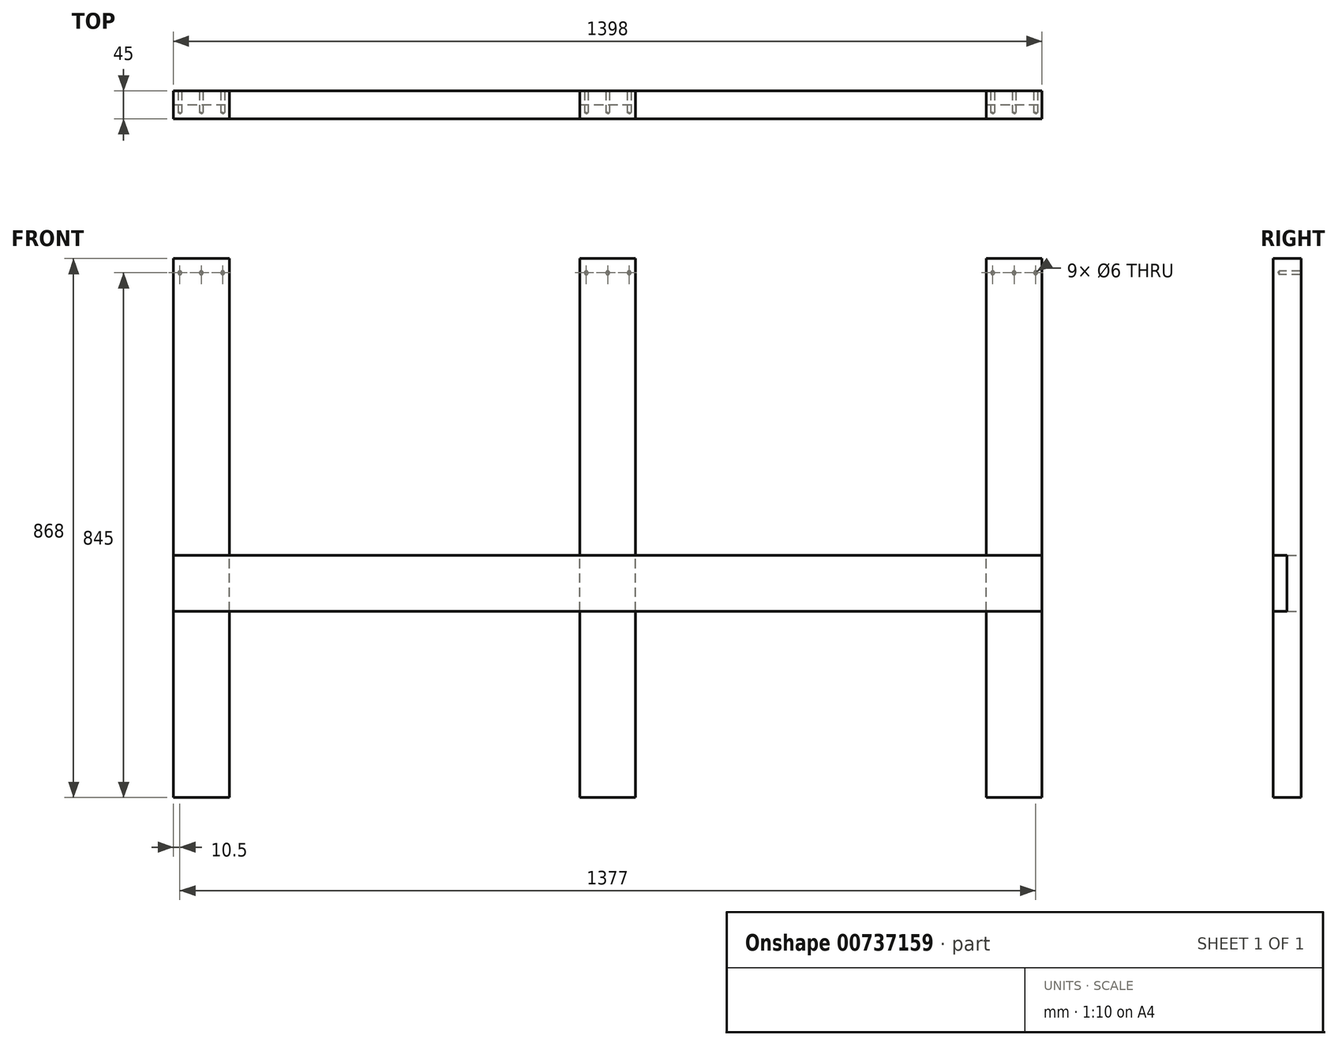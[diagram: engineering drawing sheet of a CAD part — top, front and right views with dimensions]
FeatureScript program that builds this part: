
annotation { "Feature Type Name" : "Feature", "Feature Type Description" : "" }
export const myFeature = defineFeature(function(context is Context, id is Id, definition is map)
    precondition{}
    {
        {
            var Q0;
            Q0=qCreatedBy(makeId("Front.planeOp"),FACE);
            var sketch = newSketch(context, id + "F0", { "sketchPlane" : qUnion([Q0])});
            skLineSegment(sketch, "E0.bottom", {"start": v(-609, 0) * mm, "end": v(-699, 0) * mm});
            skLineSegment(sketch, "E0.top", {"start": v(-609, 868) * mm, "end": v(-699, 868) * mm});
            skLineSegment(sketch, "E0.left", {"start": v(-609, 0) * mm, "end": v(-609, 868) * mm});
            skLineSegment(sketch, "E0.right", {"start": v(-699, 0) * mm, "end": v(-699, 868) * mm});
            skLineSegment(sketch, "E1.bottom", {"start": v(-45, 0) * mm, "end": v(45, 0) * mm});
            skLineSegment(sketch, "E1.top", {"start": v(-45, 868) * mm, "end": v(45, 868) * mm});
            skLineSegment(sketch, "E1.left", {"start": v(-45, 0) * mm, "end": v(-45, 868) * mm});
            skLineSegment(sketch, "E1.right", {"start": v(45, 0) * mm, "end": v(45, 868) * mm});
            skLineSegment(sketch, "E2.bottom", {"start": v(609, 0) * mm, "end": v(699, 0) * mm});
            skLineSegment(sketch, "E2.top", {"start": v(609, 868) * mm, "end": v(699, 868) * mm});
            skLineSegment(sketch, "E2.left", {"start": v(609, 0) * mm, "end": v(609, 868) * mm});
            skLineSegment(sketch, "E2.right", {"start": v(699, 0) * mm, "end": v(699, 868) * mm});
            skLineSegment(sketch, "E3", {"start": v(-609, 434) * mm, "end": v(-45, 434) * mm, "construction": true});
            skLineSegment(sketch, "E4", {"start": v(45, 434) * mm, "end": v(609, 434) * mm, "construction": true});
            skSolve(sketch);
        }
        {
            var Q0;
            Q0 = qSketchRegion(id + "F0", true);
            extrude(context, id + "F1", {"entities" : qUnion([Q0]), "depth" : 45 * mm, "offsetDistance" : 25 * mm});
        }
        {
            var Q0;
            Q0=makeQuery(id+"F1.opExtrude","CAP_FACE",FACE,{"disambiguationData":[OSD([sQuery(id+"F0.wireOp",EDGE,"E0.bottom"),sQuery(id+"F0.wireOp",EDGE,"E0.top"),sQuery(id+"F0.wireOp",EDGE,"E0.left"),sQuery(id+"F0.wireOp",EDGE,"E0.right")])],"isStart":false});
            var sketch = newSketch(context, id + "F2", { "sketchPlane" : qUnion([Q0])});
            skLineSegment(sketch, "E5.bottom", {"start": v(-699, 390) * mm, "end": v(699, 390) * mm});
            skLineSegment(sketch, "E5.top", {"start": v(-699, 300) * mm, "end": v(699, 300) * mm});
            skLineSegment(sketch, "E5.left", {"start": v(-699, 390) * mm, "end": v(-699, 300) * mm});
            skLineSegment(sketch, "E5.right", {"start": v(699, 390) * mm, "end": v(699, 300) * mm});
            skSolve(sketch);
        }
        {
            var Q0;
            Q0 = qSketchRegion(id + "F2", true);
            extrude(context, id + "F3", {"entities" : qUnion([Q0]), "operationType" : NewBodyOperationType.REMOVE, "oppositeDirection" : true, "depth" : (45 / 2) * mm, "offsetDistance" : 25 * mm});
        }
        {
            var Q0;
            {var subQ0=sQuery(id+"F0.wireOp",EDGE,"E0.bottom");var subQ1=sQuery(id+"F0.wireOp",EDGE,"E0.right");var subQ2=sQuery(id+"F0.wireOp",EDGE,"E0.left");Q0=makeQuery(id+"F3.boolean.opBoolean","SPLIT",FACE,{"disambiguationData":[TD([makeQuery(id+"F1.opExtrude","SWEPT_FACE",FACE,{"disambiguationData":[OSD([subQ0])]})])],"derivedFrom":makeQuery(id+"F1.opExtrude","CAP_FACE",FACE,{"disambiguationData":[OSD([subQ0,sQuery(id+"F0.wireOp",EDGE,"E0.top"),subQ2,subQ1])],"isStart":false})});}
            var sketch = newSketch(context, id + "F4", { "sketchPlane" : qUnion([Q0])});
            skLineSegment(sketch, "E6.0", {"start": v(-699, 390) * mm, "end": v(699, 390) * mm});
            skLineSegment(sketch, "E6.1", {"start": v(-699, 390) * mm, "end": v(-699, 300) * mm});
            skLineSegment(sketch, "E6.2", {"start": v(-699, 300) * mm, "end": v(699, 300) * mm});
            skLineSegment(sketch, "E6.3", {"start": v(699, 390) * mm, "end": v(699, 300) * mm});
            skSolve(sketch);
        }
        {
            var Q0;
            Q0 = qSketchRegion(id + "F4", true);
            extrude(context, id + "F5", {"entities" : qUnion([Q0]), "oppositeDirection" : true, "depth" : 45 * mm, "offsetDistance" : 25 * mm});
        }
        {
            var Q0;
            Q0=makeQuery(id+"F1.opExtrude","SWEPT_BODY",BODY,{"disambiguationData":[OSD([sQuery(id+"F0.wireOp",EDGE,"E0.bottom"),sQuery(id+"F0.wireOp",EDGE,"E0.top"),sQuery(id+"F0.wireOp",EDGE,"E0.left"),sQuery(id+"F0.wireOp",EDGE,"E0.right")])]});
            var Q1;
            Q1=makeQuery(id+"F1.opExtrude","SWEPT_BODY",BODY,{"disambiguationData":[OSD([sQuery(id+"F0.wireOp",EDGE,"E1.bottom"),sQuery(id+"F0.wireOp",EDGE,"E1.top"),sQuery(id+"F0.wireOp",EDGE,"E1.left"),sQuery(id+"F0.wireOp",EDGE,"E1.right")])]});
            var Q2;
            Q2=makeQuery(id+"F1.opExtrude","SWEPT_BODY",BODY,{"disambiguationData":[OSD([sQuery(id+"F0.wireOp",EDGE,"E2.bottom"),sQuery(id+"F0.wireOp",EDGE,"E2.top"),sQuery(id+"F0.wireOp",EDGE,"E2.left"),sQuery(id+"F0.wireOp",EDGE,"E2.right")])]});
            var Q3;
            Q3=makeQuery(id+"F5.opExtrude","SWEPT_BODY",BODY,{"disambiguationData":[OSD([sQuery(id+"F4.wireOp",EDGE,"E6.0"),sQuery(id+"F4.wireOp",EDGE,"E6.1"),sQuery(id+"F4.wireOp",EDGE,"E6.2"),sQuery(id+"F4.wireOp",EDGE,"E6.3")])]});
            booleanBodies(context, id + "F6", {"operationType" : BooleanOperationType.SUBTRACTION, "tools" : qUnion([Q0, Q1, Q2]), "targets" : qUnion([Q3]), "keepTools" : true});
        }
        {
            var Q0;
            Q0=makeQuery(id+"F1.opExtrude","CAP_FACE",FACE,{"disambiguationData":[OSD([sQuery(id+"F0.wireOp",EDGE,"E2.bottom"),sQuery(id+"F0.wireOp",EDGE,"E2.top"),sQuery(id+"F0.wireOp",EDGE,"E2.left"),sQuery(id+"F0.wireOp",EDGE,"E2.right")])],"isStart":true});
            var sketch = newSketch(context, id + "F7", { "sketchPlane" : qUnion([Q0])});
            skPoint(sketch, "E7", {"position": v(-688.5, 845) * mm});
            skPoint(sketch, "E8", {"position": v(-654, 845) * mm});
            skPoint(sketch, "E9", {"position": v(-619.5, 845) * mm});
            skPoint(sketch, "E10", {"position": v(-34.5, 845) * mm});
            skPoint(sketch, "E11", {"position": v(0, 845) * mm});
            skPoint(sketch, "E12", {"position": v(34.5, 845) * mm});
            skPoint(sketch, "E13", {"position": v(619.5, 845) * mm});
            skPoint(sketch, "E14", {"position": v(654, 845) * mm});
            skPoint(sketch, "E15", {"position": v(688.5, 845) * mm});
            skLineSegment(sketch, "E16", {"start": v(-688.5, 845) * mm, "end": v(-654, 845) * mm, "construction": true});
            skLineSegment(sketch, "E17", {"start": v(-619.5, 845) * mm, "end": v(-654, 845) * mm, "construction": true});
            skLineSegment(sketch, "E18", {"start": v(-34.5, 845) * mm, "end": v(0, 845) * mm, "construction": true});
            skLineSegment(sketch, "E19", {"start": v(34.5, 845) * mm, "end": v(0, 845) * mm, "construction": true});
            skLineSegment(sketch, "E20", {"start": v(619.5, 845) * mm, "end": v(654, 845) * mm, "construction": true});
            skLineSegment(sketch, "E21", {"start": v(654, 845) * mm, "end": v(688.5, 845) * mm, "construction": true});
            skSolve(sketch);
        }
        {
            var Q0;
            Q0=sQuery(id+"F7.wireOp",VERTEX,"E7");
            var Q1;
            Q1=sQuery(id+"F7.wireOp",VERTEX,"E8");
            var Q2;
            Q2=sQuery(id+"F7.wireOp",VERTEX,"E9");
            var Q3;
            Q3=sQuery(id+"F7.wireOp",VERTEX,"E10");
            var Q4;
            Q4=sQuery(id+"F7.wireOp",VERTEX,"E11");
            var Q5;
            Q5=sQuery(id+"F7.wireOp",VERTEX,"E12");
            var Q6;
            Q6=sQuery(id+"F7.wireOp",VERTEX,"E13");
            var Q7;
            Q7=sQuery(id+"F7.wireOp",VERTEX,"E14");
            var Q8;
            Q8=sQuery(id+"F7.wireOp",VERTEX,"E15");
            var Q9;
            Q9=makeQuery(id+"F1.opExtrude","SWEPT_BODY",BODY,{"disambiguationData":[OSD([sQuery(id+"F0.wireOp",EDGE,"E0.bottom"),sQuery(id+"F0.wireOp",EDGE,"E0.top"),sQuery(id+"F0.wireOp",EDGE,"E0.left"),sQuery(id+"F0.wireOp",EDGE,"E0.right")])]});
            var Q10;
            Q10=makeQuery(id+"F1.opExtrude","SWEPT_BODY",BODY,{"disambiguationData":[OSD([sQuery(id+"F0.wireOp",EDGE,"E1.bottom"),sQuery(id+"F0.wireOp",EDGE,"E1.top"),sQuery(id+"F0.wireOp",EDGE,"E1.left"),sQuery(id+"F0.wireOp",EDGE,"E1.right")])]});
            var Q11;
            Q11=makeQuery(id+"F1.opExtrude","SWEPT_BODY",BODY,{"disambiguationData":[OSD([sQuery(id+"F0.wireOp",EDGE,"E2.bottom"),sQuery(id+"F0.wireOp",EDGE,"E2.top"),sQuery(id+"F0.wireOp",EDGE,"E2.left"),sQuery(id+"F0.wireOp",EDGE,"E2.right")])]});
            hole(context, id + "F8", {"style" : HoleStyle.SIMPLE, "endStyle" : HoleEndStyle.BLIND, "holeDiameter" : 6 * mm, "majorDiameter" : 5 * mm, "holeDepth" : 35 * mm, "isTappedThrough" : true, "tappedDepth" : 12 * mm, "tapClearance" : 3, "locations" : qUnion([Q0, Q1, Q2, Q3, Q4, Q5, Q6, Q7, Q8]), "scope" : qUnion([Q9, Q10, Q11]), "startStyle" : HoleStartStyle.PART});
        }
    });
